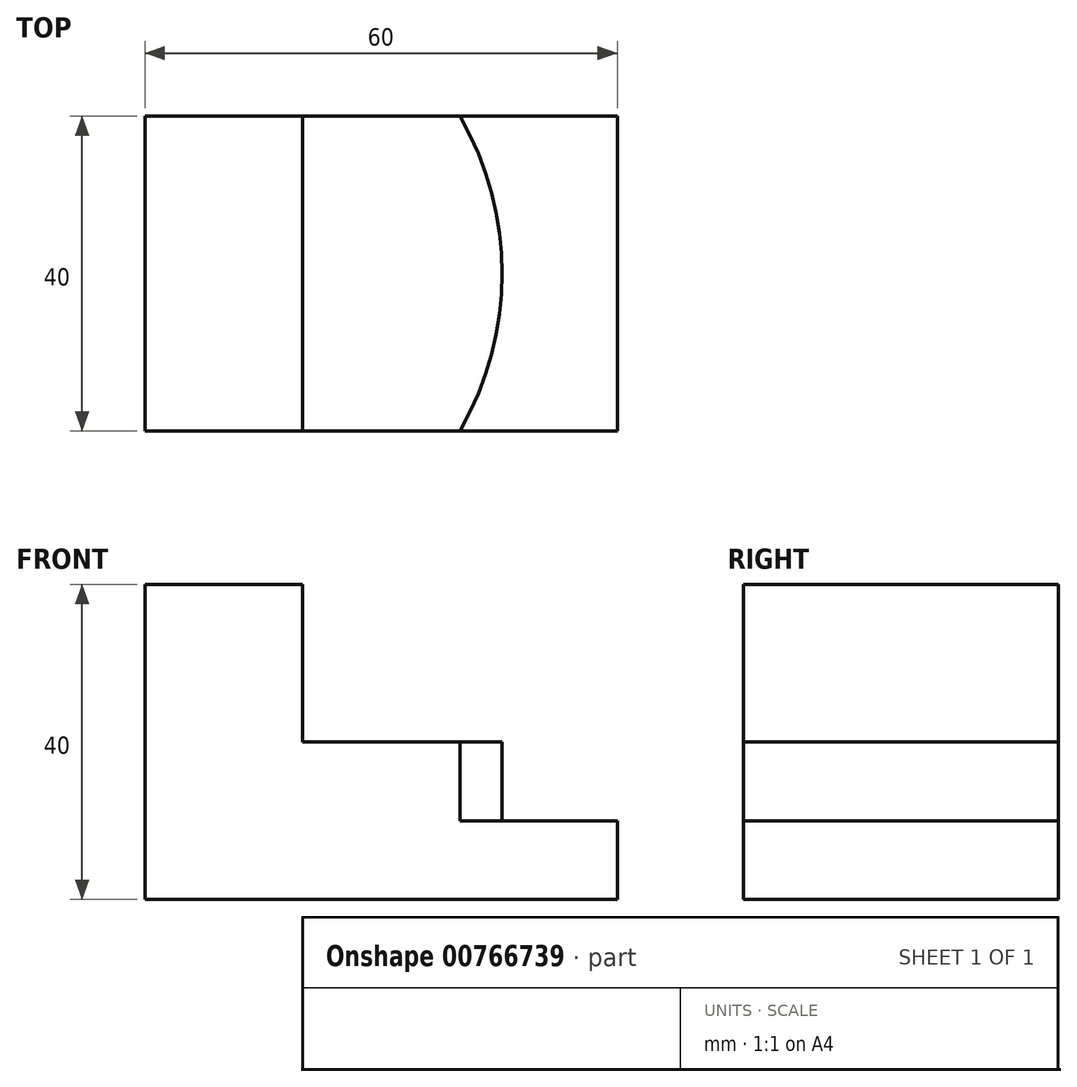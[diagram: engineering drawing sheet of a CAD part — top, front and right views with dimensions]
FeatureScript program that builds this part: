
annotation { "Feature Type Name" : "Feature", "Feature Type Description" : "" }
export const myFeature = defineFeature(function(context is Context, id is Id, definition is map)
    precondition{}
    {
        {
            var Q0;
            Q0=qCreatedBy(makeId("Front.planeOp"),FACE);
            var sketch = newSketch(context, id + "F0", { "sketchPlane" : qUnion([Q0])});
            skLineSegment(sketch, "E0", {"start": v(0, 0) * mm, "end": v(60, 0) * mm});
            skLineSegment(sketch, "E1", {"start": v(60, 0) * mm, "end": v(60, 40) * mm});
            skLineSegment(sketch, "E2", {"start": v(60, 40) * mm, "end": v(0, 40) * mm});
            skLineSegment(sketch, "E3", {"start": v(0, 40) * mm, "end": v(0, 0) * mm});
            skSolve(sketch);
        }
        {
            var Q0;
            Q0 = qSketchRegion(id + "F0", true);
            extrude(context, id + "F1", {"entities" : qUnion([Q0]), "depth" : 40 * mm, "offsetDistance" : 25 * mm});
        }
        {
            var Q0;
            Q0=makeQuery(id+"F1.opExtrude","SWEPT_FACE",FACE,{"disambiguationData":[OSD([sQuery(id+"F0.wireOp",EDGE,"E2")])]});
            var sketch = newSketch(context, id + "F2", { "sketchPlane" : qUnion([Q0])});
            skLineSegment(sketch, "E4", {"start": v(20, -40) * mm, "end": v(20, 0) * mm});
            skLineSegment(sketch, "E5", {"start": v(20, 0) * mm, "end": v(60, 0) * mm});
            skLineSegment(sketch, "E6", {"start": v(60, 0) * mm, "end": v(60, -40) * mm});
            skLineSegment(sketch, "E7", {"start": v(60, -40) * mm, "end": v(20, -40) * mm});
            skSolve(sketch);
        }
        {
            var Q0;
            Q0 = qSketchRegion(id + "F2", true);
            extrude(context, id + "F3", {"entities" : qUnion([Q0]), "operationType" : NewBodyOperationType.REMOVE, "oppositeDirection" : true, "depth" : 20 * mm, "offsetDistance" : 25 * mm});
        }
        {
            var Q0;
            Q0=makeQuery(id+"F3.boolean.opBoolean","COPY",FACE,{"derivedFrom":makeQuery(id+"F3.opExtrude","CAP_FACE",FACE,{"disambiguationData":[OSD([sQuery(id+"F2.wireOp",EDGE,"E4"),sQuery(id+"F2.wireOp",EDGE,"E5"),sQuery(id+"F2.wireOp",EDGE,"E6"),sQuery(id+"F2.wireOp",EDGE,"E7")])],"isStart":false})});
            var sketch = newSketch(context, id + "F4", { "sketchPlane" : qUnion([Q0])});
            skLineSegment(sketch, "E8", {"start": v(40, 0) * mm, "end": v(60, 0) * mm});
            skLineSegment(sketch, "E9", {"start": v(60, 0) * mm, "end": v(60, -40) * mm});
            skLineSegment(sketch, "E10", {"start": v(60, -40) * mm, "end": v(40, -40) * mm});
            skArc(sketch, "E11", {"start": v(40, -40) * mm, "mid": v(45.36, -20) * mm, "end": v(40, 0) * mm});
            skSolve(sketch);
        }
        {
            var Q0;
            Q0 = qSketchRegion(id + "F4", true);
            extrude(context, id + "F5", {"entities" : qUnion([Q0]), "operationType" : NewBodyOperationType.REMOVE, "oppositeDirection" : true, "depth" : 10 * mm, "offsetDistance" : 25 * mm});
        }
    });
